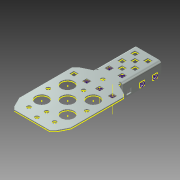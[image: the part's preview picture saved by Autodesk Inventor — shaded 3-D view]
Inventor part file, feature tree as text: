
AUTODESK INVENTOR PART (.ipt)
format: ipt  version: 2013 (Build 170138000, 138)  size: 452,608 bytes
history: native  units: in
note: dims shown in document units (in); Inventor stores cm internally (conversion verified against a paired STEP export)
features: other x14, sketch x8, sheet_metal_op x5, extrude x5
ambient origin geometry x8: Origin, YZ Plane, XZ Plane, XY Plane, X Axis, Y Axis, Z Axis, Center Point
bodies: Solid1 (feature_tree)
feature tree (32):
  sheet_metal_op  "Face1"
  sheet_metal_op  "Face2"
  sheet_metal_op  "Face3"
  other  "Corner Chamfer1"
  sketch  "Sketch7"  dims[d22=1.5in]
  sketch  "Sketch8"  dims[d23=0.046in]
  other  "Work Axis1"
  other  "Work Axis2"
  sketch  "Sketch9"  dims[d24=0.046in d25=0.023in d26=0.092in d27=0.046in d28=0.5in d29=1.5in d30=0.046in d31=0.046in d32=0.023in d33=0.092in d34=0.046in d35=0.046in d36=0.0in d37=0.125in d38=0.25in d39=45.0deg d40=0.046in d41=0.0in d42=1.0in d43=0.0in d44=1.0in d45=0.0in d46=1.0in d47=0.0in d48=1.0in d49=0.0in d50=1.0in d51=0.0in]
  sketch  "Sketch1"  dims[d1=1.1811in d3=0.7874in d5=1.5748in d7=0.3937in d8=0.5in d9=0.5in d10=0.5in d11=1.0in d12=0.25in d13=0.951in]
  other  "Plate1"
  sketch  "Sketch2"  dims[d14=1.625in d15=4.5in]
  other  "Plate2"
  sheet_metal_op  "Bend1"
  sketch  "Sketch3"  dims[d16=2.0in d17=0.163in]
  other  "Plate3"
  sheet_metal_op  "Bend2"
  sketch  "Sketch4"  dims[d18=0.182in d19=0.182in]
  sketch  "Sketch5"  dims[d20=0.046in d21=0.5in]
  other  "Srf1"
  other  "Srf2"
  other  "Srf3"
  other  "Srf4"
  other  "Srf5"
  other  "Cut1"
  other  "Cut2"
  extrude  "ExtrusionSrf1"  Depth=0.951in
  extrude  "ExtrusionSrf2"  Depth=4.5in
  extrude  "ExtrusionSrf3"  Depth=0.163in
  extrude  "ExtrusionSrf4"  Depth=0.182in
  extrude  "ExtrusionSrf5"  Depth=0.5in
  other  "Definition1"
